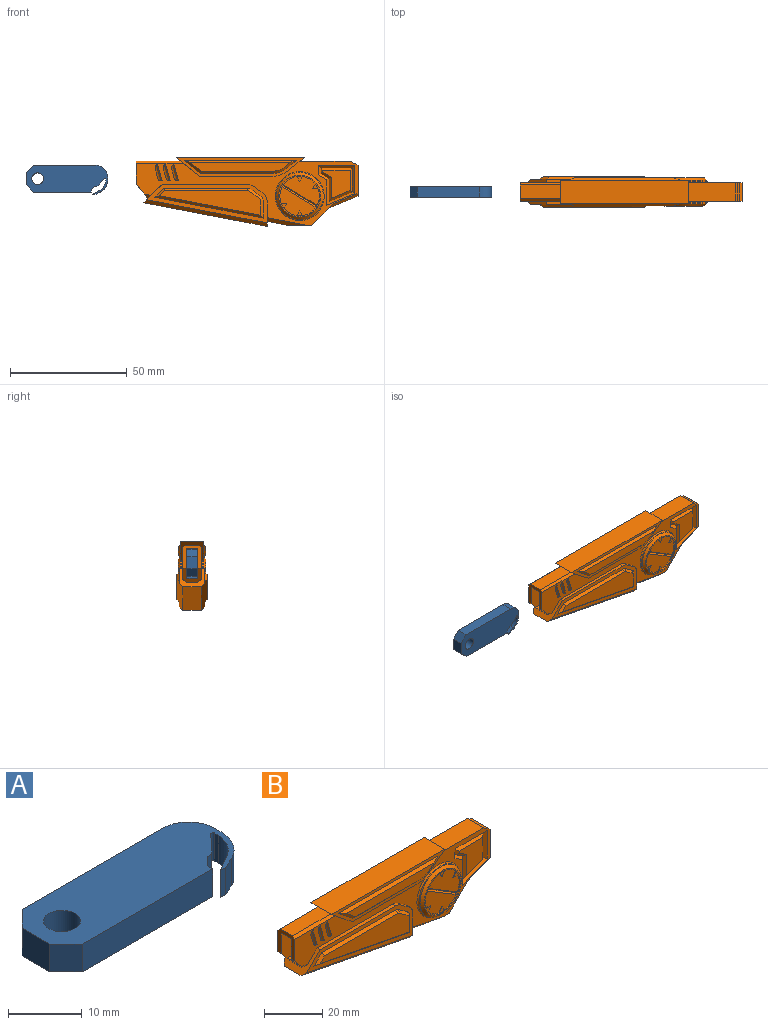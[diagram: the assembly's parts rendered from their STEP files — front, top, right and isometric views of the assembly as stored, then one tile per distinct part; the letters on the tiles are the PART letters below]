
ASSEMBLY  parts=2 mates=1
PART A: 23 faces, bbox 35x12.5x4.6 mm
  f0: plane 4.6x1.18mm, normal (1,0,0), area 5.4mm2, adj f2,f3,f10,f20
  f1: plane 1.52x0.1mm, normal (0,-1,0), area 0.2mm2, adj f2,f12,f18,f20
  f2: plane 35x11.5mm, normal (0,0,-1), area 347.5mm2, adj f0,f1,f4,f5,f6,f7,f8,f9
  f3: plane 35x12.54mm, normal (0,0,1), area 348.8mm2, adj f0,f4,f5,f6,f7,f8,f9,f10
  f4: plane 24.96x4.6mm, normal (0,-1,0), area 114.8mm2, adj f2,f3,f7,f11
  f5: plane 26.9x4.6mm, normal (0,1,0), area 123.7mm2, adj f2,f3,f8,f10
  f6: plane 5.3x4.6mm, normal (-1,0,0), area 24.4mm2, adj f2,f3,f7,f8
  f7: plane 4.6x3.1mm, normal (-0.71,-0.71,0), area 20.2mm2, adj f2,f3,f4,f6
  f8: plane 4.6x3.1mm, normal (-0.71,0.71,0), area 20.2mm2, adj f2,f3,f5,f6
  f9: cylinder r=2.5mm len=5mm, axis (0,0,1), area 72.3mm2, adj f2,f3
  f10: cylinder r=5mm len=5mm, axis (0,0,1), area 36.1mm2, adj f0,f2,f3,f5
  f11: plane 4.6x1.01mm, normal (1,0,0), area 4.6mm2, adj f2,f3,f4,f21
  f12: plane 4.6x3.11mm, normal (-0.51,0.86,0), area 16.4mm2, adj f1,f2,f3,f17,f18,f19
  f13: plane 4.6x3.4mm, normal (0.73,-0.69,0), area 21.5mm2, adj f2,f3,f14,f22
  f14: plane 4.6x0.87mm, normal (0,-1,0), area 4mm2, adj f2,f3,f13,f21
  f15: plane 4.6x0.79mm, normal (-1,0.05,0), area 3.7mm2, adj f2,f3,f19,f22
  f16: plane 4.5x1.98mm, normal (0.42,-0.91,0), area 9.8mm2, adj f3,f17,f18,f20
  f17: plane 4.5x1mm, normal (-0.04,-1,0), area 4.5mm2, adj f3,f12,f16,f18
  f18: plane 3.21x1.04mm, normal (0,0,-1), area 1.3mm2, adj f1,f12,f16,f17,f20
  f19: cylinder r=5mm len=4.6mm, axis (0,0,1), area 22.7mm2, adj f2,f3,f12,f15
  f20: cylinder r=6mm len=5.44mm, axis (0,0,-1), area 31.3mm2, adj f0,f1,f2,f3,f16,f18
  f21: plane 4.6x1.5mm, normal (0.71,-0.71,0), area 9.8mm2, adj f2,f3,f11,f14
  f22: cylinder r=0.3mm len=4.6mm, axis (0,0,1), area 3.4mm2, adj f2,f3,f13,f15
PART B: 194 faces, bbox 95x13x29.5 mm
  f0: plane 12.5x6mm, normal (0.38,0,-0.92), area 29.2mm2, adj f1,f2,f89,f169,f179,f180,f181
  f1: plane 13x8mm, normal (1,0,0), area 52.9mm2, adj f0,f4,f5,f89,f169,f174,f179,f180
  f2: plane 9.17x9.17mm, normal (0.71,0,-0.71), area 40.7mm2, adj f0,f3,f4,f5,f89,f169,f176,f177
  f3: plane 10.36x8mm, normal (0,0,-1), area 23.8mm2, adj f2,f4,f5,f9,f19,f104,f176,f177
  f4: plane 95x27.5mm, normal (0,-1,0), area 619.7mm2, adj f1,f2,f3,f10,f11,f13,f14,f16
  f5: plane 95x27.5mm, normal (0,1,0), area 619.7mm2, adj f1,f2,f3,f10,f11,f16,f23,f76
  f6: plane 18.88x6mm, normal (0,0,1), area 113.2mm2, adj f11,f78,f90,f170
  f7: cylinder r=8.5mm len=17mm, axis (0,-1,0), area 24.8mm2, adj f8,f25,f46,f49,f50,f51,f52,f53
  f8: plane 15.51x12.37mm, normal (0,-1,0), area 99.8mm2, adj f7,f55,f56,f58,f59,f61
  f9: plane 8.82x5mm, normal (-0.19,0,-0.98), area 44.9mm2, adj f3,f16,f19,f104
  f10: plane 21.88x8mm, normal (0,0,1), area 175mm2, adj f4,f5,f80,f175
  f11: plane 10x8mm, normal (-1,0,0), area 36.5mm2, adj f4,f5,f6,f76,f90,f91,f93,f170
  f12: plane 5x0.12mm, normal (-0.19,0,-0.98), area 0.6mm2, adj f20,f23,f76,f105
  f13: plane 4.28x3.06mm, normal (0.58,0,0.81), area 7.9mm2, adj f4,f17,f21,f22
  f14: plane 36.72x1.5mm, normal (0,0,1), area 55.1mm2, adj f4,f17,f21,f23
  f15: plane 52.82x10.18mm, normal (-0.19,0,-0.98), area 430.3mm2, adj f16,f18,f23,f103
  f16: plane 11x10.94mm, normal (1,0,0), area 50.4mm2, adj f4,f5,f9,f15,f17,f18,f19,f22
  f17: plane 51.53x16.47mm, normal (0,-1,0), area 190.6mm2, adj f13,f14,f16,f18,f21,f22,f23,f39
  f18: plane 52.82x11.47mm, normal (-0.13,-0.71,-0.69), area 112.7mm2, adj f15,f16,f17,f23
  f19: plane 16.74x3.23mm, normal (-0.13,-0.71,-0.69), area 27.6mm2, adj f3,f4,f9,f16
  f20: plane 2.9x1.84mm, normal (-0.13,-0.71,-0.69), area 3.3mm2, adj f4,f12,f23,f76
  f21: cylinder r=4mm len=2.33mm, axis (0,-1,0), area 3.7mm2, adj f4,f13,f14,f17
  f22: cylinder r=4mm len=3.26mm, axis (0,-1,0), area 5.7mm2, adj f4,f13,f16,f17
  f23: plane 11x7.82mm, normal (-0.71,0,0.71), area 54mm2, adj f4,f5,f12,f14,f15,f17,f18,f20
  f24: cylinder r=10mm len=20mm, axis (0,-1,0), area 31.4mm2, adj f47,f48
  f25: plane 18x18mm, normal (0,-1,0), area 27.5mm2, adj f7,f47
  f26: plane 4.08x1.15mm, normal (0.96,0,0.27), area 4.2mm2, adj f4,f32,f33,f189
  f27: plane 0.38x0.37mm, normal (0,0,1), area 0.1mm2, adj f4,f32,f186
  f28: plane 4.08x1.15mm, normal (0.96,0,0.27), area 4.2mm2, adj f4,f34,f35,f188
  f29: plane 0.38x0.37mm, normal (0,0,1), area 0.1mm2, adj f4,f35,f187
  f30: plane 4.08x1.15mm, normal (0.96,0,0.27), area 4.2mm2, adj f4,f36,f37,f190
  f31: plane 0.38x0.37mm, normal (0,0,1), area 0.1mm2, adj f4,f36,f185
  f32: cylinder r=1.5mm len=1.44mm, axis (0,1,0), area 1.6mm2, adj f4,f26,f27,f186,f189
  f33: cylinder r=1.5mm len=1.84mm, axis (0,1,0), area 1.7mm2, adj f4,f26,f186,f189
  f34: cylinder r=1.5mm len=1.84mm, axis (0,1,0), area 1.7mm2, adj f4,f28,f187,f188
  f35: cylinder r=1.5mm len=1.44mm, axis (0,1,0), area 1.6mm2, adj f4,f28,f29,f187,f188
  f36: cylinder r=1.5mm len=1.44mm, axis (0,1,0), area 1.6mm2, adj f4,f30,f31,f185,f190
  f37: cylinder r=1.5mm len=1.84mm, axis (0,1,0), area 1.7mm2, adj f4,f30,f185,f190
  f38: plane 43.33x10.5mm, normal (0,-1,0), area 262.1mm2, adj f39,f40,f41,f42,f43,f44,f45
  f39: plane 36.01x1mm, normal (0,-0.71,0.71), area 50.6mm2, adj f17,f38,f40,f41
  f40: cone r=1.3mm half-angle=45deg, axis (0,1,0), area 1.6mm2, adj f17,f38,f39,f42
  f41: plane 4.19x3.77mm, normal (-0.5,-0.71,0.5), area 5.9mm2, adj f17,f38,f39,f43
  f42: plane 4.86x3.87mm, normal (0.41,-0.71,0.58), area 7.4mm2, adj f17,f38,f40,f44
  f43: plane 46.37x9.57mm, normal (-0.13,-0.71,-0.69), area 64.6mm2, adj f17,f38,f41,f45
  f44: cone r=1.3mm half-angle=45deg, axis (0,1,0), area 2.4mm2, adj f17,f38,f42,f45
  f45: plane 7.35x1mm, normal (0.71,-0.71,0), area 9.5mm2, adj f17,f38,f43,f44
  f46: plane 15.51x12.37mm, normal (0,-1,0), area 99.8mm2, adj f7,f49,f50,f52,f53,f62
  f47: cone r=9mm half-angle=45deg, axis (0,1,0), area 84.4mm2, adj f24,f25
  f48: torus R=10.5mm, axis (0,-1,0), area 50.2mm2, adj f4,f24
  f49: plane 2.07x1.19mm, normal (-0.87,0,0.5), area 0.6mm2, adj f7,f46,f50,f51
  f50: plane 2.38x0.25mm, normal (0,0,-1), area 0.6mm2, adj f7,f46,f49,f51
  f51: plane 2.38x2.07mm, normal (0,-1,0), area 2.6mm2, adj f7,f49,f50
  f52: plane 2.07x1.19mm, normal (-0.87,0,-0.5), area 0.6mm2, adj f7,f46,f53,f54
  f53: plane 2.07x1.19mm, normal (0.87,0,-0.5), area 0.6mm2, adj f7,f46,f52,f54
  f54: plane 2.38x2.15mm, normal (0,-1,0), area 2.6mm2, adj f7,f52,f53
  f55: plane 2.07x1.19mm, normal (0.87,0,-0.5), area 0.6mm2, adj f7,f8,f56,f57
  f56: plane 2.38x0.25mm, normal (0,0,1), area 0.6mm2, adj f7,f8,f55,f57
  f57: plane 2.38x2.07mm, normal (0,-1,0), area 2.6mm2, adj f7,f55,f56
  f58: plane 2.07x1.19mm, normal (0.87,0,0.5), area 0.6mm2, adj f7,f8,f59,f60
  f59: plane 2.07x1.19mm, normal (-0.87,0,0.5), area 0.6mm2, adj f7,f8,f58,f60
  f60: plane 2.38x2.15mm, normal (0,-1,0), area 2.6mm2, adj f7,f58,f59
  f61: plane 14.81x9.19mm, normal (0.36,-0.71,0.61), area 12mm2, adj f7,f8,f62
  f62: plane 14.81x9.19mm, normal (-0.36,-0.71,-0.61), area 12mm2, adj f7,f46,f61
  f63: plane 4.06x1mm, normal (0.71,-0.71,0), area 4.6mm2, adj f4,f64,f65,f75
  f64: plane 15.61x1mm, normal (0,-0.71,-0.71), area 20.7mm2, adj f4,f63,f66,f73
  f65: plane 4.52x2.73mm, normal (0.37,-0.71,0.6), area 5.9mm2, adj f4,f63,f67,f74
  f66: plane 12.13x1mm, normal (-0.71,-0.71,0), area 16mm2, adj f4,f64,f68,f71
  f67: plane 11.46x1mm, normal (0.71,-0.71,0), area 14.8mm2, adj f4,f65,f68,f72
  f68: plane 12.09x5.68mm, normal (-0.27,-0.71,0.65), area 17mm2, adj f4,f66,f67,f70
  f69: plane 12.14x11.61mm, normal (0,-1,0), area 91.8mm2, adj f70,f71,f72,f73,f74,f75
  f70: plane 10.09x4.85mm, normal (0.27,-0.71,-0.65), area 13.9mm2, adj f68,f69,f71,f72
  f71: plane 10.46x1mm, normal (0.71,-0.71,0), area 13.6mm2, adj f66,f69,f70,f73
  f72: plane 10.53x1mm, normal (-0.71,-0.71,0), area 13.4mm2, adj f67,f69,f70,f74
  f73: plane 13.61x1mm, normal (0,-0.71,0.71), area 17.8mm2, adj f64,f69,f71,f75
  f74: plane 4.52x2.73mm, normal (-0.37,-0.71,-0.6), area 5.9mm2, adj f65,f69,f72,f75
  f75: plane 2.5x1mm, normal (-0.71,-0.71,0), area 2.4mm2, adj f63,f69,f73,f74
  f76: plane 8x5.95mm, normal (-0.77,0,-0.64), area 35.5mm2, adj f4,f5,f11,f12,f20,f92,f93,f105
  f77: plane 55x10mm, normal (0,0,1), area 550mm2, adj f78,f80,f81,f161
  f78: plane 10x10mm, normal (-0.62,0,-0.78), area 46.4mm2, adj f4,f5,f6,f77,f79,f81,f90,f160
  f79: plane 31.49x1mm, normal (0,0,-1), area 31.5mm2, adj f4,f78,f81,f82
  f80: plane 10x7.26mm, normal (0.62,0,-0.78), area 37.8mm2, adj f4,f5,f10,f77,f81,f82,f161,f162
  f81: plane 55x8mm, normal (0,-1,0), area 129.2mm2, adj f77,f78,f79,f80,f82,f84,f85,f86
  f82: cylinder r=10mm len=6.25mm, axis (0,-1,0), area 6.7mm2, adj f4,f79,f80,f81
  f83: plane 42.46x3.6mm, normal (0,-1,0), area 135.8mm2, adj f84,f85,f86,f87,f88
  f84: plane 31.07x1mm, normal (0,-0.71,-0.71), area 43.7mm2, adj f81,f83,f85,f86
  f85: plane 7.35x5.6mm, normal (-0.44,-0.71,-0.55), area 10.4mm2, adj f81,f83,f84,f87
  f86: cone r=7.8mm half-angle=45deg, axis (0,1,0), area 7.9mm2, adj f81,f83,f84,f88
  f87: plane 48.16x1mm, normal (0,-0.71,0.71), area 64.1mm2, adj f81,f83,f85,f88
  f88: plane 5.21x3.67mm, normal (0.44,-0.71,-0.55), area 6.3mm2, adj f81,f83,f86,f87
  f89: plane 12.5x6.26mm, normal (0.27,-0.71,-0.65), area 17.7mm2, adj f0,f1,f2,f4
  f90: plane 20.13x1mm, normal (0,-0.71,0.71), area 27.6mm2, adj f4,f6,f11,f78
  f91: plane 25x5mm, normal (0,0,-1), area 125mm2, adj f11,f93,f94,f171
  f92: plane 22.11x5mm, normal (0,0,1), area 73.1mm2, adj f76,f93,f94,f96,f97,f171,f172
  f93: plane 25x12mm, normal (0,1,0), area 294.9mm2, adj f11,f76,f91,f92,f94
  f94: plane 14.5x5mm, normal (-1,0,0), area 67.5mm2, adj f91,f92,f93,f95,f97,f171,f172
  f95: plane 15x3mm, normal (0,0,1), area 45mm2, adj f94,f96,f97,f172
  f96: plane 3x2.5mm, normal (0.71,0,-0.71), area 10.6mm2, adj f92,f95,f97,f172
  f97: plane 15x2.5mm, normal (0,1,0), area 34.4mm2, adj f92,f94,f95,f96
  f98: cylinder r=8.5mm len=17mm, axis (0,1,0), area 24.8mm2, adj f99,f109,f130,f133,f134,f135,f136,f137
  f99: plane 15.51x12.37mm, normal (0,1,0), area 99.8mm2, adj f98,f139,f140,f142,f143,f145
  f100: plane 4.28x3.06mm, normal (0.58,0,0.81), area 7.9mm2, adj f5,f102,f106,f107
  f101: plane 36.72x1.5mm, normal (0,0,1), area 55.1mm2, adj f5,f23,f102,f106
  f102: plane 51.53x16.47mm, normal (0,1,0), area 190.6mm2, adj f16,f23,f100,f101,f103,f106,f107,f123
  f103: plane 52.82x11.47mm, normal (-0.13,0.71,-0.69), area 112.7mm2, adj f15,f16,f23,f102
  f104: plane 16.74x3.23mm, normal (-0.13,0.71,-0.69), area 27.6mm2, adj f3,f5,f9,f16
  f105: plane 2.9x1.84mm, normal (-0.13,0.71,-0.69), area 3.3mm2, adj f5,f12,f23,f76
  f106: cylinder r=4mm len=2.33mm, axis (0,1,0), area 3.7mm2, adj f5,f100,f101,f102
  f107: cylinder r=4mm len=3.26mm, axis (0,1,0), area 5.7mm2, adj f5,f16,f100,f102
  f108: cylinder r=10mm len=20mm, axis (0,1,0), area 31.4mm2, adj f131,f132
  f109: plane 18x18mm, normal (0,1,0), area 27.5mm2, adj f98,f131
  f110: plane 4.08x1.15mm, normal (0.96,0,0.27), area 4.2mm2, adj f5,f116,f117,f191
  f111: plane 0.38x0.37mm, normal (0,0,1), area 0.1mm2, adj f5,f116,f184
  f112: plane 4.08x1.15mm, normal (0.96,0,0.27), area 4.2mm2, adj f5,f118,f119,f192
  f113: plane 0.38x0.37mm, normal (0,0,1), area 0.1mm2, adj f5,f119,f183
  f114: plane 4.08x1.15mm, normal (0.96,0,0.27), area 4.2mm2, adj f5,f120,f121,f193
  f115: plane 0.38x0.37mm, normal (0,0,1), area 0.1mm2, adj f5,f120,f182
  f116: cylinder r=1.5mm len=1.44mm, axis (0,-1,0), area 1.6mm2, adj f5,f110,f111,f184,f191
  f117: cylinder r=1.5mm len=1.84mm, axis (0,-1,0), area 1.7mm2, adj f5,f110,f184,f191
  f118: cylinder r=1.5mm len=1.84mm, axis (0,-1,0), area 1.7mm2, adj f5,f112,f183,f192
  f119: cylinder r=1.5mm len=1.44mm, axis (0,-1,0), area 1.6mm2, adj f5,f112,f113,f183,f192
  f120: cylinder r=1.5mm len=1.44mm, axis (0,-1,0), area 1.6mm2, adj f5,f114,f115,f182,f193
  f121: cylinder r=1.5mm len=1.84mm, axis (0,-1,0), area 1.7mm2, adj f5,f114,f182,f193
  f122: plane 43.33x10.5mm, normal (0,1,0), area 262.1mm2, adj f123,f124,f125,f126,f127,f128,f129
  f123: plane 36.01x1mm, normal (0,0.71,0.71), area 50.6mm2, adj f102,f122,f124,f125
  f124: cone r=1.3mm half-angle=45deg, axis (0,-1,0), area 1.6mm2, adj f102,f122,f123,f126
  f125: plane 4.19x3.77mm, normal (-0.5,0.71,0.5), area 5.9mm2, adj f102,f122,f123,f127
  f126: plane 4.86x3.87mm, normal (0.41,0.71,0.58), area 7.4mm2, adj f102,f122,f124,f128
  f127: plane 46.37x9.57mm, normal (-0.13,0.71,-0.69), area 64.6mm2, adj f102,f122,f125,f129
  f128: cone r=1.3mm half-angle=45deg, axis (0,-1,0), area 2.4mm2, adj f102,f122,f126,f129
  f129: plane 7.35x1mm, normal (0.71,0.71,0), area 9.5mm2, adj f102,f122,f127,f128
  f130: plane 15.51x12.37mm, normal (0,1,0), area 99.8mm2, adj f98,f133,f134,f136,f137,f146
  f131: cone r=9mm half-angle=45deg, axis (0,-1,0), area 84.4mm2, adj f108,f109
  f132: torus R=10.5mm, axis (0,1,0), area 50.2mm2, adj f5,f108
  f133: plane 2.07x1.19mm, normal (-0.87,0,0.5), area 0.6mm2, adj f98,f130,f134,f135
  f134: plane 2.38x0.25mm, normal (0,0,-1), area 0.6mm2, adj f98,f130,f133,f135
  f135: plane 2.38x2.07mm, normal (0,1,0), area 2.6mm2, adj f98,f133,f134
  f136: plane 2.07x1.19mm, normal (-0.87,0,-0.5), area 0.6mm2, adj f98,f130,f137,f138
  f137: plane 2.07x1.19mm, normal (0.87,0,-0.5), area 0.6mm2, adj f98,f130,f136,f138
  f138: plane 2.38x2.15mm, normal (0,1,0), area 2.6mm2, adj f98,f136,f137
  f139: plane 2.07x1.19mm, normal (0.87,0,-0.5), area 0.6mm2, adj f98,f99,f140,f141
  f140: plane 2.38x0.25mm, normal (0,0,1), area 0.6mm2, adj f98,f99,f139,f141
  f141: plane 2.38x2.07mm, normal (0,1,0), area 2.6mm2, adj f98,f139,f140
  f142: plane 2.07x1.19mm, normal (0.87,0,0.5), area 0.6mm2, adj f98,f99,f143,f144
  f143: plane 2.07x1.19mm, normal (-0.87,0,0.5), area 0.6mm2, adj f98,f99,f142,f144
  f144: plane 2.38x2.15mm, normal (0,1,0), area 2.6mm2, adj f98,f142,f143
  f145: plane 14.81x9.19mm, normal (0.36,0.71,0.61), area 12mm2, adj f98,f99,f146
  f146: plane 14.81x9.19mm, normal (-0.36,0.71,-0.61), area 12mm2, adj f98,f130,f145
  f147: plane 4.06x1mm, normal (0.71,0.71,0), area 4.6mm2, adj f5,f148,f149,f159
  f148: plane 15.61x1mm, normal (0,0.71,-0.71), area 20.7mm2, adj f5,f147,f150,f157
  f149: plane 4.52x2.73mm, normal (0.37,0.71,0.6), area 5.9mm2, adj f5,f147,f151,f158
  f150: plane 12.13x1mm, normal (-0.71,0.71,0), area 16mm2, adj f5,f148,f152,f155
  f151: plane 11.46x1mm, normal (0.71,0.71,0), area 14.8mm2, adj f5,f149,f152,f156
  f152: plane 12.09x5.68mm, normal (-0.27,0.71,0.65), area 17mm2, adj f5,f150,f151,f154
  f153: plane 12.14x11.61mm, normal (0,1,0), area 91.8mm2, adj f154,f155,f156,f157,f158,f159
  f154: plane 10.09x4.85mm, normal (0.27,0.71,-0.65), area 13.9mm2, adj f152,f153,f155,f156
  f155: plane 10.46x1mm, normal (0.71,0.71,0), area 13.6mm2, adj f150,f153,f154,f157
  f156: plane 10.53x1mm, normal (-0.71,0.71,0), area 13.4mm2, adj f151,f153,f154,f158
  f157: plane 13.61x1mm, normal (0,0.71,0.71), area 17.8mm2, adj f148,f153,f155,f159
  f158: plane 4.52x2.73mm, normal (-0.37,0.71,-0.6), area 5.9mm2, adj f149,f153,f156,f159
  f159: plane 2.5x1mm, normal (-0.71,0.71,0), area 2.4mm2, adj f147,f153,f157,f158
  f160: plane 31.49x1mm, normal (0,0,-1), area 31.5mm2, adj f5,f78,f161,f162
  f161: plane 55x8mm, normal (0,1,0), area 129.2mm2, adj f77,f78,f80,f160,f162,f164,f165,f166
  f162: cylinder r=10mm len=6.25mm, axis (0,1,0), area 6.7mm2, adj f5,f80,f160,f161
  f163: plane 42.46x3.6mm, normal (0,1,0), area 135.8mm2, adj f164,f165,f166,f167,f168
  f164: plane 31.07x1mm, normal (0,0.71,-0.71), area 43.7mm2, adj f161,f163,f165,f166
  f165: plane 7.35x5.6mm, normal (-0.44,0.71,-0.55), area 10.4mm2, adj f161,f163,f164,f167
  f166: cone r=7.8mm half-angle=45deg, axis (0,-1,0), area 7.9mm2, adj f161,f163,f164,f168
  f167: plane 48.16x1mm, normal (0,0.71,0.71), area 64.1mm2, adj f161,f163,f165,f168
  f168: plane 5.21x3.67mm, normal (0.44,0.71,-0.55), area 6.3mm2, adj f161,f163,f166,f167
  f169: plane 12.5x6.26mm, normal (0.27,0.71,-0.65), area 17.7mm2, adj f0,f1,f2,f5
  f170: plane 20.13x1mm, normal (0,0.71,0.71), area 27.6mm2, adj f5,f6,f11,f78
  f171: plane 25x12mm, normal (0,-1,0), area 294.9mm2, adj f11,f76,f91,f92,f94
  f172: plane 15x2.5mm, normal (0,-1,0), area 34.4mm2, adj f92,f94,f95,f96
  f173: plane 8x1mm, normal (0,0,1), area 8mm2, adj f4,f5,f174,f175
  f174: plane 8x1mm, normal (0.71,0,0.71), area 11.3mm2, adj f1,f4,f5,f173
  f175: plane 8x1mm, normal (0.71,0,0.71), area 11.3mm2, adj f4,f5,f10,f173
  f176: cylinder r=8.5mm len=16.51mm, axis (0,1,0), area 137.1mm2, adj f2,f3,f177,f178
  f177: plane 16.51x12mm, normal (0,1,0), area 149.4mm2, adj f2,f3,f176
  f178: plane 16.51x12mm, normal (0,-1,0), area 149.4mm2, adj f2,f3,f176
  f179: cylinder r=8.5mm len=15.8mm, axis (0,1,0), area 139mm2, adj f0,f1,f180,f181
  f180: plane 15.8x13.75mm, normal (0,1,0), area 170.8mm2, adj f0,f1,f179
  f181: plane 15.8x13.75mm, normal (0,-1,0), area 170.8mm2, adj f0,f1,f179
  f182: plane 7.02x2.39mm, normal (-0.68,0.71,-0.19), area 4.6mm2, adj f5,f115,f120,f121,f193
  f183: plane 7.02x2.39mm, normal (-0.68,0.71,-0.19), area 4.6mm2, adj f5,f113,f118,f119,f192
  f184: plane 7.02x2.39mm, normal (-0.68,0.71,-0.19), area 4.6mm2, adj f5,f111,f116,f117,f191
  f185: plane 7.02x2.39mm, normal (-0.68,-0.71,-0.19), area 4.6mm2, adj f4,f31,f36,f37,f190
  f186: plane 7.02x2.39mm, normal (-0.68,-0.71,-0.19), area 4.6mm2, adj f4,f27,f32,f33,f189
  f187: plane 7.02x2.39mm, normal (-0.68,-0.71,-0.19), area 4.6mm2, adj f4,f29,f34,f35,f188
  f188: cylinder r=2mm len=7.07mm, axis (0.27,0,-0.96), area 7.3mm2, adj f28,f34,f35,f187
  f189: cylinder r=2mm len=7.07mm, axis (0.27,0,-0.96), area 7.3mm2, adj f26,f32,f33,f186
  f190: cylinder r=2mm len=7.07mm, axis (0.27,0,-0.96), area 7.3mm2, adj f30,f36,f37,f185
  f191: cylinder r=2mm len=7.07mm, axis (-0.27,0,0.96), area 7.3mm2, adj f110,f116,f117,f184
  f192: cylinder r=2mm len=7.07mm, axis (-0.27,0,0.96), area 7.3mm2, adj f112,f118,f119,f183
  f193: cylinder r=2mm len=7.07mm, axis (-0.27,0,0.96), area 7.3mm2, adj f114,f120,f121,f182
PLACE A rot(axis=(1,0,0),90deg) t=(-39.26,-1.5,-7.56)mm
PLACE B t=(38.06,4,-7.5)mm
MATE slider A.f0 <-> B.f94  axis (1,0,0) through (-21.76,0,-6.81)mm
